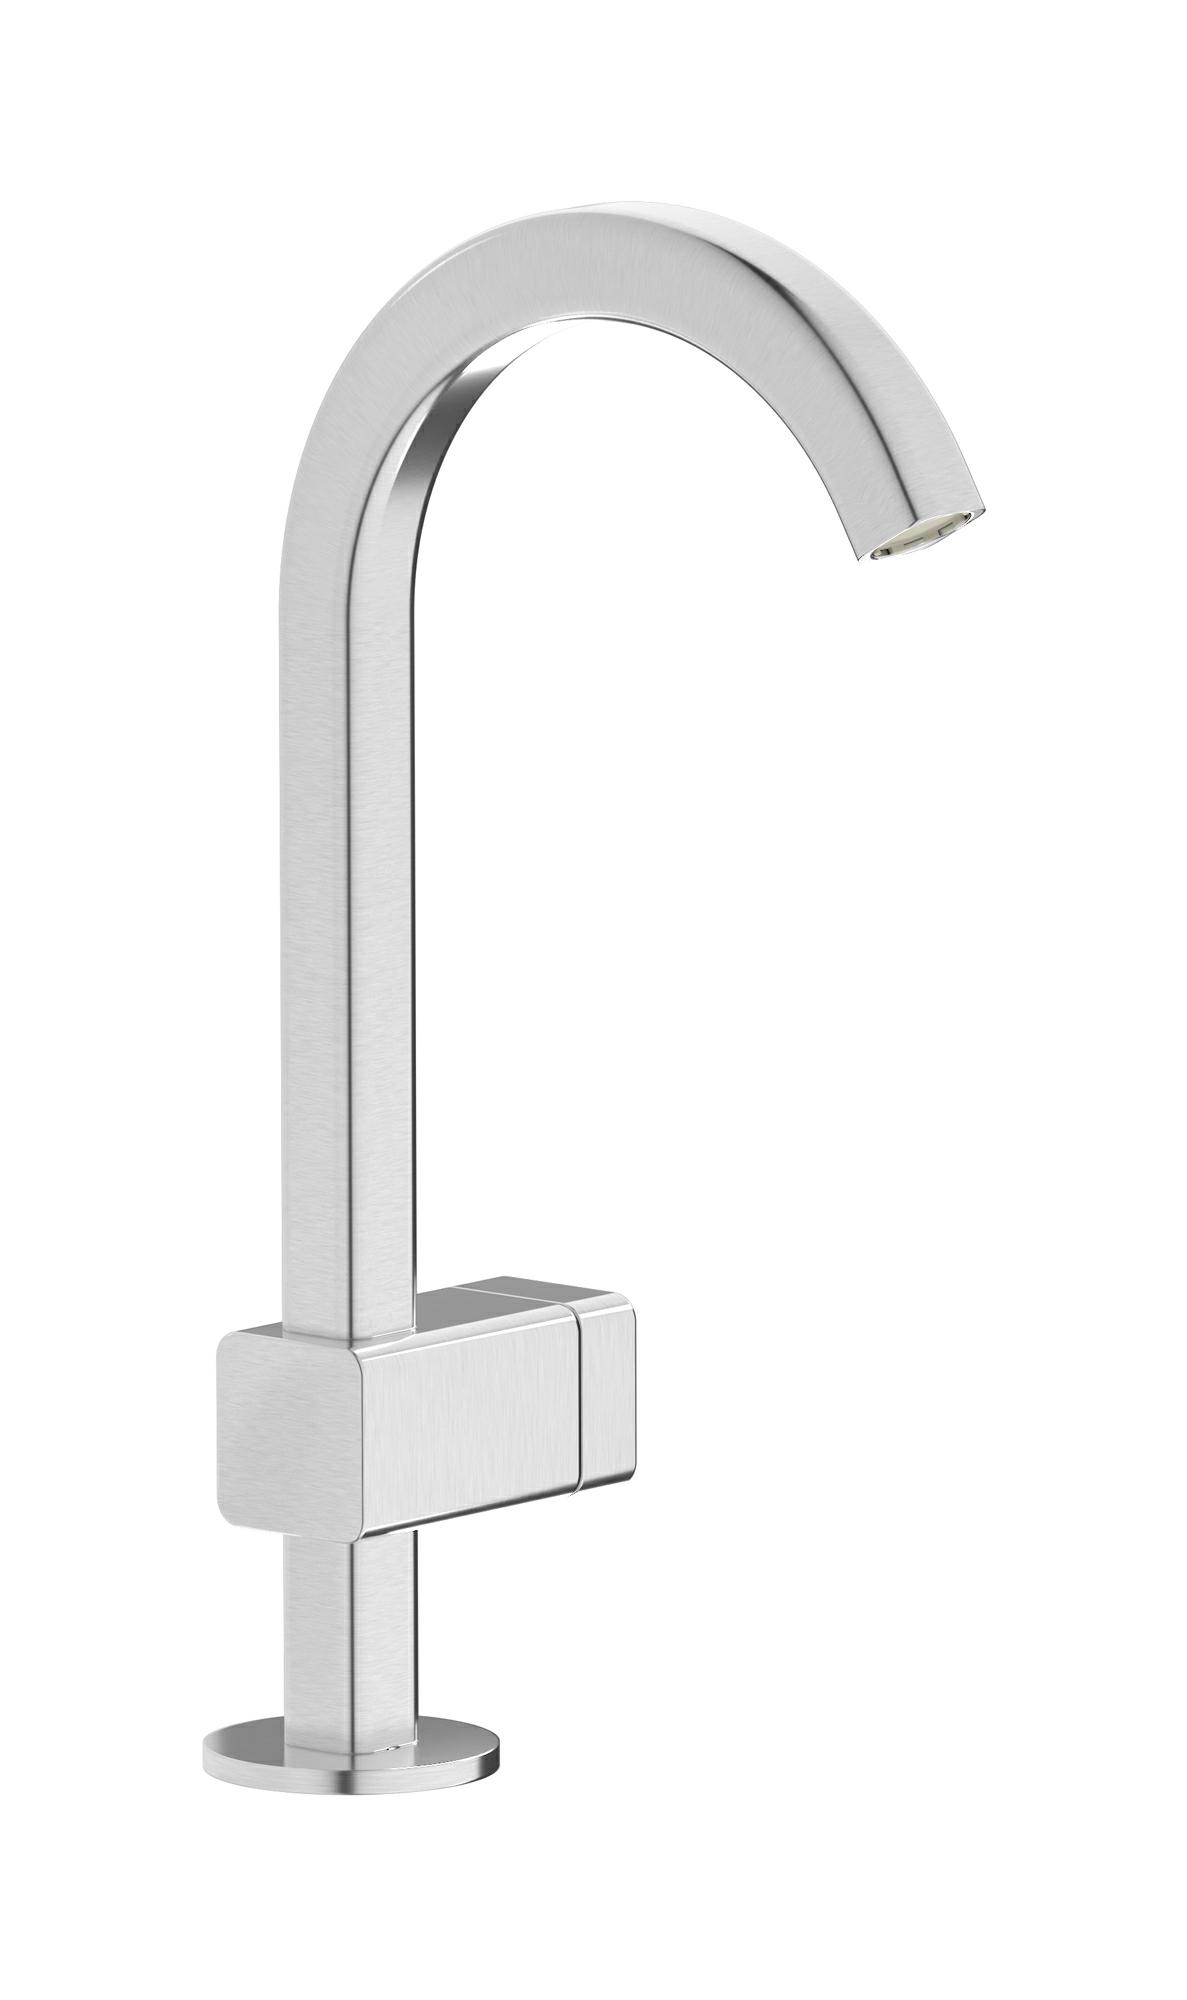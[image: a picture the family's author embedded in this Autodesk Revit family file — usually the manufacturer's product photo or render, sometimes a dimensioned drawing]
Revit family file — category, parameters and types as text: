
# Revit family: EO200_1
name_source: partatom
category: Apparecchi idraulici
units: mm (PartAtom-declared; Revit-internal decimal feet)

## family parameters
Basato su piano di lavoro = No
Condiviso = No
Mantieni orientamento annotazione = No
Numero OmniClass = 23.45.55.17
Punto di calcolo locali = No
Quota connettore circolare = Usa diametro
Sempre verticale = Sì
Taglio con vuoti quando caricato = No
Tipo di parte = Normale
Titolo OmniClass = Mixing Faucets

## types (12) — shared parameters
Cold water inlet = 10 mm  [stored 0.0328084 ft]
Commenti sul tipo = Basin mixer
Connessione CW = No
Connessione HW = No
Connessione di scarico = No
Connessione di ventilazione = No
Descrizione = Washbasin monohole mixer
Hot water inlet = 10 mm  [stored 0.0328084 ft]
Produttore = IB Rubinetterie S.p.A.
URL = https://www.weareib.it
zero-valued in all types: Prospetto di default

## per-type parameters (varying)
| type | Finishes surface | Immagine tipo | Modello |
| Chrome | IB_Chrome | EO200CC_1.jpg | EO200CC_1 |
| Brushed nickel | IB_Brushed nickel | EO200SS_1.jpg | EO200SS_1 |
| Natural brass | IB_Brass | EO200ON_1.jpg | EO200ON_1 |
| Matt black | IB_matt black | EO200NP_1.jpg | EO200NP_1 |
| Black chrome | IB_Black chrome | EO200CF_1.jpg | EO200CF_1 |
| Brushed black chrome | IB_Brushed black chrome | EO200CS_1.jpg | EO200CS_1 |
| Pale gold | IB_Pale gold | EO200II_1.jpg | EO200II_1 |
| Brushed pale gold | IB_brushed pale gold | EO200IS_1.jpg | EO200IS_1 |
| Rose gold | IB_Rose gold | EO200RS_1.jpg | EO200RS_1 |
| Brushed rose gold | IB_Brushed rose gold | EO200SR_1.jpg | EO200SR_1 |
| Gold | IB_gold | EO200OO_1.jpg | EO200OO_1 |
| Brushed gold | IB_brushed gold | EO200OS_1.jpg | EO200OS_1 |

note: [stored X ft] marks values corroborated as IEEE doubles in the binary element streams (Revit-internal decimal feet)
